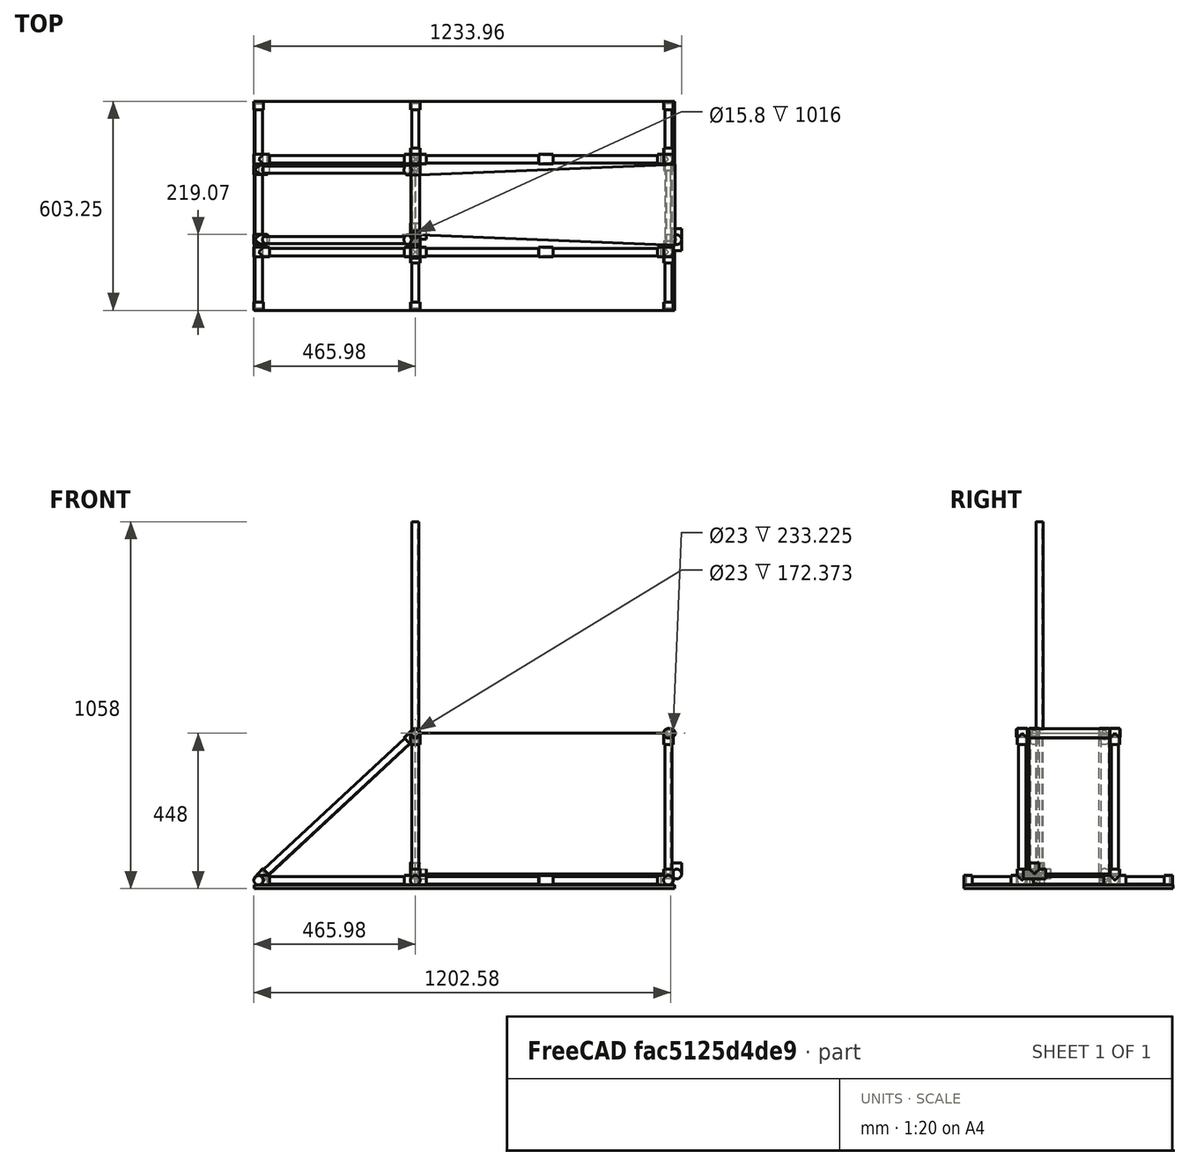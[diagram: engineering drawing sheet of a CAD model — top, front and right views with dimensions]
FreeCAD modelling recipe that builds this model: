
FCSTD DOCUMENT  (FreeCAD 0.19R24291 (Git))
Label: Xtracycle solar
License: All rights reserved
LicenseURL: http://en.wikipedia.org/wiki/All_rights_reserved
objects: Part::Cylinder×81, Part::MultiFuse×25, Part::Cut×3, Part::Box×1, Part::Wedge×1
note: 111 computed .brp shape members not serialized (recipe doc carries the construction recipe); baked Part::Feature solids carry a one-line shape summary decoded from their .brp

FEATURE [Part::Cylinder] Cylinder
  Angle = 360
  AttacherType = Attacher::AttachEngine3D
  Height = 300
  Placement = pos=(0,-68,406) rot=(-1,0,0;1.5708rad)
  Radius = 11.5
FEATURE [Part::Cylinder] Cylinder001
  Angle = 360
  AttacherType = Attacher::AttachEngine3D
  Height = 171.45
  Placement = pos=(0,8.5e-14,406) rot=(-1,0,0;1.5708rad)
  Radius = 13
FEATURE [Part::Box] Box001  label="Solar panel"
  AttacherType = Attacher::AttachEngine3D
  Height = 10
  Length = 1212.85
  Placement = pos=(-465,-219.075,-42) rot=(0,0,1;0rad)
  Width = 603.25
FEATURE [Part::Cylinder] Cylinder002
  Angle = 360
  AttacherType = Attacher::AttachEngine3D
  Height = 1016
  Radius = 7.9
FEATURE [Part::Cylinder] Cylinder003
  Angle = 360
  AttacherType = Attacher::AttachEngine3D
  Height = 1016
  Radius = 10.67
FEATURE [Part::Cut] Cut001  label="Pipe"
  Base = -> Cylinder003
  Tool = -> Cylinder002
FEATURE [Part::Cylinder] Cylinder004
  Angle = 360
  AttacherType = Attacher::AttachEngine3D
  Height = 32.1945
  Radius = 13.9827
FEATURE [Part::Cylinder] Cylinder005
  Angle = 360
  AttacherType = Attacher::AttachEngine3D
  Height = 28.0162
  Placement = pos=(0,14.0081,0) rot=(1,0,0;1.5708rad)
  Radius = 13.9827
FEATURE [Part::MultiFuse] Fusion001  label="Slip"
  Shapes = -> [Cylinder004,Cylinder005]
FEATURE [Part::Cylinder] Cylinder006
  Angle = 360
  AttacherType = Attacher::AttachEngine3D
  Height = 31.877
  Radius = 13.9827
FEATURE [Part::Cylinder] Cylinder007
  Angle = 360
  AttacherType = Attacher::AttachEngine3D
  Height = 64.36
  Placement = pos=(0,32.1818,0) rot=(1,0,0;1.5708rad)
  Radius = 13.9827
FEATURE [Part::MultiFuse] Fusion002  label="T"
  Shapes = -> [Cylinder006,Cylinder007]
FEATURE [Part::Cylinder] Cylinder008
  Angle = 360
  AttacherType = Attacher::AttachEngine3D
  Height = 31.877
  Radius = 13.9827
FEATURE [Part::Cylinder] Cylinder009
  Angle = 360
  AttacherType = Attacher::AttachEngine3D
  Height = 64.36
  Placement = pos=(0,32.1818,0) rot=(1,0,0;1.5708rad)
  Radius = 13.9827
FEATURE [Part::MultiFuse] Fusion003  label="T001"
  Shapes = -> [Cylinder008,Cylinder009]
FEATURE [Part::Cylinder] Cylinder010
  Angle = 360
  AttacherType = Attacher::AttachEngine3D
  Height = 31.877
  Placement = pos=(0,0,0) rot=(0,1,0;1.5708rad)
  Radius = 13.9827
FEATURE [Part::MultiFuse] Fusion004  label="4-way"
  Shapes = -> [Fusion003,Cylinder010]
FEATURE [Part::Cylinder] Cylinder011
  Angle = 360
  AttacherType = Attacher::AttachEngine3D
  Height = 64.36
  Placement = pos=(0,32.1818,0) rot=(1,0,0;1.5708rad)
  Radius = 13.9827
FEATURE [Part::Cylinder] Cylinder012
  Angle = 360
  AttacherType = Attacher::AttachEngine3D
  Height = 31.877
  Placement = pos=(0,0,0) rot=(0,1,0;1.5708rad)
  Radius = 13.9827
FEATURE [Part::Cylinder] Cylinder013
  Angle = 360
  AttacherType = Attacher::AttachEngine3D
  Height = 64.36
  Placement = pos=(0,0,-32.18) rot=(0,0,1;1.5708rad)
  Radius = 13.9827
FEATURE [Part::MultiFuse] Fusion005  label="5-Way"
  Shapes = -> [Cylinder012,Cylinder013,Cylinder011]
FEATURE [Part::Cylinder] Cylinder014
  Angle = 360
  AttacherType = Attacher::AttachEngine3D
  Height = 64.36
  Placement = pos=(0,32.1818,0) rot=(1,0,0;1.5708rad)
  Radius = 13.9827
FEATURE [Part::Cylinder] Cylinder015
  Angle = 360
  AttacherType = Attacher::AttachEngine3D
  Height = 31.877
  Placement = pos=(0,0,0) rot=(0,1,0;1.5708rad)
  Radius = 13.9827
FEATURE [Part::Cylinder] Cylinder016
  Angle = 360
  AttacherType = Attacher::AttachEngine3D
  Height = 31.877
  Radius = 13.9827
FEATURE [Part::MultiFuse] Fusion006  label="T002"
  Shapes = -> [Cylinder016,Cylinder014]
FEATURE [Part::MultiFuse] Fusion007  label="4-way001"
  Placement = pos=(754,-15,1.67e-13) rot=(0,-1,0;1.5708rad)
  Shapes = -> [Fusion006,Cylinder015]
FEATURE [Part::Wedge] Wedge
  AttacherType = Attacher::AttachEngine3D
  Placement = pos=(737,202,2.08e-13) rot=(0.57735,-0.57735,0.57735;2.0944rad)
  X2max = 406.4
  X2min = 0
  Xmax = 406.4
  Xmin = 0
  Ymax = 736.6
  Ymin = 0
  Z2max = 202.22
  Z2min = 30.775
  Zmax = 233
  Zmin = 0
FEATURE [Part::MultiFuse] Fusion
  Shapes = -> [Cylinder001,Wedge]
FEATURE [Part::Cut] Cut
  Base = -> Fusion
  Tool = -> Cylinder
FEATURE [Part::Cylinder] Cylinder017
  Angle = 360
  AttacherType = Attacher::AttachEngine3D
  Height = 300
  Placement = pos=(0,-68,406) rot=(-1,0,0;1.5708rad)
  Radius = 11.5
FEATURE [Part::Cylinder] Cylinder019
  Angle = 360
  AttacherType = Attacher::AttachEngine3D
  Height = 300
  Placement = pos=(736.6,-57,406) rot=(-1,0,0;1.5708rad)
  Radius = 11.5
FEATURE [Part::Cylinder] Cylinder018
  Angle = 360
  AttacherType = Attacher::AttachEngine3D
  Height = 233
  Placement = pos=(736.6,-30.775,406) rot=(-1,0,0;1.5708rad)
  Radius = 13
FEATURE [Part::MultiFuse] Fusion008
  Shapes = -> [Cut,Cylinder018]
FEATURE [Part::Cut] Cut002  label="Xtracycle"
  Base = -> Fusion008
  Tool = -> Cylinder019
FEATURE [Part::Cylinder] Cylinder020
  Angle = 360
  AttacherType = Attacher::AttachEngine3D
  Height = 64.36
  Placement = pos=(0,32.1818,0) rot=(1,0,0;1.5708rad)
  Radius = 13.9827
FEATURE [Part::Cylinder] Cylinder021
  Angle = 360
  AttacherType = Attacher::AttachEngine3D
  Height = 31.877
  Placement = pos=(0,0,0) rot=(0,1,0;1.5708rad)
  Radius = 13.9827
FEATURE [Part::Cylinder] Cylinder022
  Angle = 360
  AttacherType = Attacher::AttachEngine3D
  Height = 31.877
  Radius = 13.9827
FEATURE [Part::MultiFuse] Fusion009  label="T003"
  Shapes = -> [Cylinder022,Cylinder020]
FEATURE [Part::MultiFuse] Fusion010  label="Front 4-way L"
  Placement = pos=(730.25,-50.3,-18) rot=(0,-1,0;1.5708rad)
  Shapes = -> [Fusion009,Cylinder021]
FEATURE [Part::Cylinder] Cylinder023
  Angle = 360
  AttacherType = Attacher::AttachEngine3D
  Height = 32.1945
  Radius = 13.9827
FEATURE [Part::Cylinder] Cylinder024
  Angle = 360
  AttacherType = Attacher::AttachEngine3D
  Height = 28.0162
  Placement = pos=(0,14.0081,0) rot=(1,0,0;1.5708rad)
  Radius = 13.9827
FEATURE [Part::MultiFuse] Fusion011  label="Front Slip L"
  Placement = pos=(730.25,-50.3,406) rot=(0,1,0;3.14159rad)
  Shapes = -> [Cylinder023,Cylinder024]
FEATURE [Part::Cylinder] Cylinder025
  Angle = 360
  AttacherType = Attacher::AttachEngine3D
  Height = 28.0162
  Placement = pos=(0,14.0081,0) rot=(1,0,0;1.5708rad)
  Radius = 13.9827
FEATURE [Part::Cylinder] Cylinder026
  Angle = 360
  AttacherType = Attacher::AttachEngine3D
  Height = 32.1945
  Radius = 13.9827
FEATURE [Part::MultiFuse] Fusion012  label="Front Slip R"
  Placement = pos=(730.25,217,406) rot=(0,1,0;3.14159rad)
  Shapes = -> [Cylinder026,Cylinder025]
FEATURE [Part::Cylinder] Cylinder027  label="Front Riser L"
  Angle = 360
  AttacherType = Attacher::AttachEngine3D
  Height = 400.05
  Placement = pos=(730.25,-50,0) rot=(0,0,1;0rad)
  Radius = 10.62
FEATURE [Part::Cylinder] Cylinder028  label="Front Riser R"
  Angle = 360
  AttacherType = Attacher::AttachEngine3D
  Height = 400.05
  Placement = pos=(730.25,217,0) rot=(0,0,1;0rad)
  Radius = 10.62
FEATURE [Part::Cylinder] Cylinder029
  Angle = 360
  AttacherType = Attacher::AttachEngine3D
  Height = 64.36
  Placement = pos=(0,32.1818,0) rot=(1,0,0;1.5708rad)
  Radius = 13.9827
FEATURE [Part::Cylinder] Cylinder030
  Angle = 360
  AttacherType = Attacher::AttachEngine3D
  Height = 31.877
  Placement = pos=(0,0,0) rot=(0,1,0;1.5708rad)
  Radius = 13.9827
FEATURE [Part::Cylinder] Cylinder031
  Angle = 360
  AttacherType = Attacher::AttachEngine3D
  Height = 31.877
  Radius = 13.9827
FEATURE [Part::MultiFuse] Fusion014  label="T004"
  Shapes = -> [Cylinder031,Cylinder029]
FEATURE [Part::MultiFuse] Fusion013  label="Front 4-way R"
  Placement = pos=(730.25,217,-18) rot=(0,-1,0;1.5708rad)
  Shapes = -> [Fusion014,Cylinder030]
FEATURE [Part::Cylinder] Cylinder032  label="Front middle cross"
  Angle = 360
  AttacherType = Attacher::AttachEngine3D
  Height = 241.3
  Placement = pos=(730.25,204.3,-18) rot=(1,0,0;1.5708rad)
  Radius = 10.62
FEATURE [Part::Cylinder] Cylinder033  label="Front span R"
  Angle = 360
  AttacherType = Attacher::AttachEngine3D
  Height = 349.25
  Placement = pos=(709,217.3,-18) rot=(0.57735,-0.57735,-0.57735;2.0944rad)
  Radius = 10.62
FEATURE [Part::Cylinder] Cylinder034  label="Front span L"
  Angle = 360
  AttacherType = Attacher::AttachEngine3D
  Height = 349.25
  Placement = pos=(709,-50.7,-18) rot=(0.57735,-0.57735,-0.57735;2.0944rad)
  Radius = 10.62
FEATURE [Part::Cylinder] Cylinder035
  Angle = 360
  AttacherType = Attacher::AttachEngine3D
  Height = 64.36
  Placement = pos=(0,0,-32.18) rot=(0,0,1;1.5708rad)
  Radius = 13.9827
FEATURE [Part::Cylinder] Cylinder036
  Angle = 360
  AttacherType = Attacher::AttachEngine3D
  Height = 64.36
  Placement = pos=(0,32.1818,0) rot=(1,0,0;1.5708rad)
  Radius = 13.9827
FEATURE [Part::Cylinder] Cylinder037
  Angle = 360
  AttacherType = Attacher::AttachEngine3D
  Height = 31.877
  Placement = pos=(0,0,0) rot=(0,1,0;1.5708rad)
  Radius = 13.9827
FEATURE [Part::MultiFuse] Fusion015  label="5-Way001"
  Placement = pos=(0,-50.3,-18) rot=(0,-1,0;1.5708rad)
  Shapes = -> [Cylinder037,Cylinder035,Cylinder036]
FEATURE [Part::Cylinder] Cylinder038
  Angle = 360
  AttacherType = Attacher::AttachEngine3D
  Height = 64.36
  Placement = pos=(0,0,-32.18) rot=(0,0,1;1.5708rad)
  Radius = 13.9827
FEATURE [Part::Cylinder] Cylinder039
  Angle = 360
  AttacherType = Attacher::AttachEngine3D
  Height = 64.36
  Placement = pos=(0,32.1818,0) rot=(1,0,0;1.5708rad)
  Radius = 13.9827
FEATURE [Part::Cylinder] Cylinder040
  Angle = 360
  AttacherType = Attacher::AttachEngine3D
  Height = 31.877
  Placement = pos=(0,0,0) rot=(0,1,0;1.5708rad)
  Radius = 13.9827
FEATURE [Part::MultiFuse] Fusion016  label="5-Way002"
  Placement = pos=(-2.1e-15,217,-18) rot=(0,-1,0;1.5708rad)
  Shapes = -> [Cylinder040,Cylinder038,Cylinder039]
FEATURE [Part::Cylinder] Cylinder043
  Angle = 360
  AttacherType = Attacher::AttachEngine3D
  Height = 32.1945
  Radius = 13.9827
FEATURE [Part::Cylinder] Cylinder044
  Angle = 360
  AttacherType = Attacher::AttachEngine3D
  Height = 28.0162
  Placement = pos=(0,14.0081,0) rot=(1,0,0;1.5708rad)
  Radius = 13.9827
FEATURE [Part::MultiFuse] Fusion017  label="Middle inner slip L"
  Placement = pos=(-5e-14,-15,406) rot=(0,1,0;3.92699rad)
  Shapes = -> [Cylinder043,Cylinder044]
FEATURE [Part::Cylinder] Cylinder045
  Angle = 360
  AttacherType = Attacher::AttachEngine3D
  Height = 32.1945
  Radius = 13.9827
FEATURE [Part::Cylinder] Cylinder046
  Angle = 360
  AttacherType = Attacher::AttachEngine3D
  Height = 28.0162
  Placement = pos=(0,14.0081,0) rot=(1,0,0;1.5708rad)
  Radius = 13.9827
FEATURE [Part::MultiFuse] Fusion018  label="Middle inner slip R"
  Placement = pos=(-5e-14,186,406) rot=(0,1,0;3.92699rad)
  Shapes = -> [Cylinder045,Cylinder046]
FEATURE [Part::Cylinder] Cylinder047
  Angle = 360
  AttacherType = Attacher::AttachEngine3D
  Height = 32.1945
  Radius = 13.9827
FEATURE [Part::Cylinder] Cylinder048
  Angle = 360
  AttacherType = Attacher::AttachEngine3D
  Height = 28.0162
  Placement = pos=(0,14.0081,0) rot=(1,0,0;1.5708rad)
  Radius = 13.9827
FEATURE [Part::MultiFuse] Fusion019  label="Middle outer slip L"
  Placement = pos=(-5e-14,-50,406) rot=(0,1,0;3.14159rad)
  Shapes = -> [Cylinder047,Cylinder048]
FEATURE [Part::Cylinder] Cylinder049
  Angle = 360
  AttacherType = Attacher::AttachEngine3D
  Height = 32.1945
  Radius = 13.9827
FEATURE [Part::Cylinder] Cylinder050
  Angle = 360
  AttacherType = Attacher::AttachEngine3D
  Height = 28.0162
  Placement = pos=(0,14.0081,0) rot=(1,0,0;1.5708rad)
  Radius = 13.9827
FEATURE [Part::MultiFuse] Fusion020  label="Middle outer slip R"
  Placement = pos=(-5e-14,217,406) rot=(0,1,0;3.14159rad)
  Shapes = -> [Cylinder049,Cylinder050]
FEATURE [Part::Cylinder] Cylinder053  label="Rear riser L"
  Angle = 360
  AttacherType = Attacher::AttachEngine3D
  Height = 593.725
  Placement = pos=(0.275283,-16,405.959) rot=(0,1,0;3.96364rad)
  Radius = 10.62
FEATURE [Part::Cylinder] Cylinder055  label="Rear riser R"
  Angle = 360
  AttacherType = Attacher::AttachEngine3D
  Height = 593.725
  Placement = pos=(-9.24449,187,395.561) rot=(0,1,0;3.96364rad)
  Radius = 10.62
FEATURE [Part::Cylinder] Cylinder056  label="Rear span R"
  Angle = 360
  AttacherType = Attacher::AttachEngine3D
  Height = 425.45
  Placement = pos=(-1,217.3,-18) rot=(0.57735,-0.57735,-0.57735;2.0944rad)
  Radius = 10.62
FEATURE [Part::Cylinder] Cylinder057  label="Rear span L"
  Angle = 360
  AttacherType = Attacher::AttachEngine3D
  Height = 425.45
  Placement = pos=(-15,-50.7,-18) rot=(0.57735,-0.57735,-0.57735;2.0944rad)
  Radius = 10.62
FEATURE [Part::Cylinder] Cylinder061
  Angle = 360
  AttacherType = Attacher::AttachEngine3D
  Height = 32.1945
  Radius = 13.9827
FEATURE [Part::Cylinder] Cylinder062
  Angle = 360
  AttacherType = Attacher::AttachEngine3D
  Height = 28.0162
  Placement = pos=(0,14.0081,0) rot=(1,0,0;1.5708rad)
  Radius = 13.9827
FEATURE [Part::MultiFuse] Fusion023  label="Rear outer slip L"
  Placement = pos=(-452,-51,-18) rot=(0,1,0;1.5708rad)
  Shapes = -> [Cylinder061,Cylinder062]
FEATURE [Part::Cylinder] Cylinder063
  Angle = 360
  AttacherType = Attacher::AttachEngine3D
  Height = 32.1945
  Radius = 13.9827
FEATURE [Part::Cylinder] Cylinder064
  Angle = 360
  AttacherType = Attacher::AttachEngine3D
  Height = 28.0162
  Placement = pos=(0,14.0081,0) rot=(1,0,0;1.5708rad)
  Radius = 13.9827
FEATURE [Part::MultiFuse] Fusion024  label="Rear outer slip R"
  Placement = pos=(-452,217,-18) rot=(0,1,0;1.5708rad)
  Shapes = -> [Cylinder063,Cylinder064]
FEATURE [Part::Cylinder] Cylinder065
  Angle = 360
  AttacherType = Attacher::AttachEngine3D
  Height = 32.1945
  Radius = 13.9827
FEATURE [Part::Cylinder] Cylinder066
  Angle = 360
  AttacherType = Attacher::AttachEngine3D
  Height = 28.0162
  Placement = pos=(0,14.0081,0) rot=(1,0,0;1.5708rad)
  Radius = 13.9827
FEATURE [Part::MultiFuse] Fusion025  label="Rear Inner slip R"
  Placement = pos=(-452,187,-18) rot=(0,1,0;0.748746rad)
  Shapes = -> [Cylinder065,Cylinder066]
FEATURE [Part::Cylinder] Cylinder067
  Angle = 360
  AttacherType = Attacher::AttachEngine3D
  Height = 32.1945
  Radius = 13.9827
FEATURE [Part::Cylinder] Cylinder068
  Angle = 360
  AttacherType = Attacher::AttachEngine3D
  Height = 28.0162
  Placement = pos=(0,14.0081,0) rot=(1,0,0;1.5708rad)
  Radius = 13.9827
FEATURE [Part::MultiFuse] Fusion026  label="Rear inner slip L"
  Placement = pos=(-452,-14,-18) rot=(0,1,0;0.748746rad)
  Shapes = -> [Cylinder067,Cylinder068]
FEATURE [Part::Cylinder] Cylinder072  label="Middle middle cross"
  Angle = 360
  AttacherType = Attacher::AttachEngine3D
  Height = 241.3
  Placement = pos=(1.25,204.3,-18) rot=(1,0,0;1.5708rad)
  Radius = 10.62
FEATURE [Part::Cylinder] Cylinder073  label="Rear middle cross"
  Angle = 360
  AttacherType = Attacher::AttachEngine3D
  Height = 589
  Placement = pos=(-451.75,376.3,-18) rot=(1,0,0;1.5708rad)
  Radius = 10.62
FEATURE [Part::Cylinder] Cylinder074  label="Front Frame"
  Angle = 360
  AttacherType = Attacher::AttachEngine3D
  Height = 295.275
  Placement = pos=(730.25,231.3,406) rot=(1,0,0;1.5708rad)
  Radius = 10.62
FEATURE [Part::Cylinder] Cylinder075  label="Middle Riser L"
  Angle = 360
  AttacherType = Attacher::AttachEngine3D
  Height = 400.05
  Placement = pos=(0,-50,0) rot=(0,0,1;0rad)
  Radius = 10.62
FEATURE [Part::Cylinder] Cylinder076  label="Middle Riser R"
  Angle = 360
  AttacherType = Attacher::AttachEngine3D
  Height = 400.05
  Placement = pos=(0,217,0) rot=(0,0,1;0rad)
  Radius = 10.62
FEATURE [Part::Cylinder] Cylinder077  label="Rear Frame"
  Angle = 360
  AttacherType = Attacher::AttachEngine3D
  Height = 295.275
  Placement = pos=(0,231.3,406) rot=(1,0,0;1.5708rad)
  Radius = 10.62
FEATURE [Part::Cylinder] Cylinder078  label="Front right cross"
  Angle = 360
  AttacherType = Attacher::AttachEngine3D
  Height = 146.05
  Placement = pos=(730.25,377.3,-18) rot=(1,0,0;1.5708rad)
  Radius = 10.62
FEATURE [Part::Cylinder] Cylinder079  label="Front left cross"
  Angle = 360
  AttacherType = Attacher::AttachEngine3D
  Height = 146.05
  Placement = pos=(730.25,-66.7,-18) rot=(1,0,0;1.5708rad)
  Radius = 10.62
FEATURE [Part::Cylinder] Cylinder080  label="Middle right cross"
  Angle = 360
  AttacherType = Attacher::AttachEngine3D
  Height = 146.05
  Placement = pos=(0,377.3,-18) rot=(1,0,0;1.5708rad)
  Radius = 10.62
FEATURE [Part::Cylinder] Cylinder081  label="Middle left cross"
  Angle = 360
  AttacherType = Attacher::AttachEngine3D
  Height = 146.05
  Placement = pos=(0,-66.7,-18) rot=(1,0,0;1.5708rad)
  Radius = 10.62
FEATURE [Part::Cylinder] Cylinder082  label="Middle span R"
  Angle = 360
  AttacherType = Attacher::AttachEngine3D
  Height = 349.25
  Placement = pos=(356,217.3,-18) rot=(0.57735,-0.57735,-0.57735;2.0944rad)
  Radius = 10.62
FEATURE [Part::Cylinder] Cylinder083  label="Middle span L"
  Angle = 360
  AttacherType = Attacher::AttachEngine3D
  Height = 349.25
  Placement = pos=(356,-50.7,-18) rot=(0.57735,-0.57735,-0.57735;2.0944rad)
  Radius = 10.62
FEATURE [Part::Cylinder] Cylinder084  label="Coupling L"
  Angle = 360
  AttacherType = Attacher::AttachEngine3D
  Height = 42.037
  Placement = pos=(356,-50.7,-18) rot=(0,1,0;1.5708rad)
  Radius = 13.9827
FEATURE [Part::Cylinder] Cylinder085  label="Coupling R"
  Angle = 360
  AttacherType = Attacher::AttachEngine3D
  Height = 42.037
  Placement = pos=(356,217.3,-18) rot=(0,1,0;1.5708rad)
  Radius = 13.9827
FEATURE [Part::Cylinder] Cylinder086  label="End cap front R"
  Angle = 360
  AttacherType = Attacher::AttachEngine3D
  Height = 23.4442
  Placement = pos=(730,383.3,-18) rot=(1,0,0;1.5708rad)
  Radius = 13.9827
FEATURE [Part::Cylinder] Cylinder087  label="End cap middle R"
  Angle = 360
  AttacherType = Attacher::AttachEngine3D
  Height = 23.4442
  Placement = pos=(0,383.3,-18) rot=(1,0,0;1.5708rad)
  Radius = 13.9827
FEATURE [Part::Cylinder] Cylinder088  label="End cap rear R"
  Angle = 360
  AttacherType = Attacher::AttachEngine3D
  Height = 23.4442
  Placement = pos=(-452,383.3,-18) rot=(1,0,0;1.5708rad)
  Radius = 13.9827
FEATURE [Part::Cylinder] Cylinder089  label="End cap front L"
  Angle = 360
  AttacherType = Attacher::AttachEngine3D
  Height = 23.4442
  Placement = pos=(730,-194.7,-18) rot=(1,0,0;1.5708rad)
  Radius = 13.9827
FEATURE [Part::Cylinder] Cylinder090  label="End cap middle L"
  Angle = 360
  AttacherType = Attacher::AttachEngine3D
  Height = 23.4442
  Placement = pos=(0,-194.7,-18) rot=(1,0,0;1.5708rad)
  Radius = 13.9827
FEATURE [Part::Cylinder] Cylinder091  label="End cap rear L"
  Angle = 360
  AttacherType = Attacher::AttachEngine3D
  Height = 23.4442
  Placement = pos=(-452,-194.7,-18) rot=(1,0,0;1.5708rad)
  Radius = 13.9827
